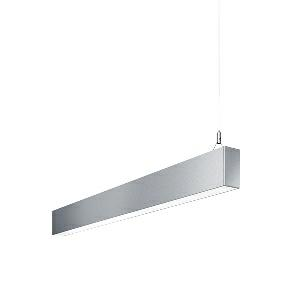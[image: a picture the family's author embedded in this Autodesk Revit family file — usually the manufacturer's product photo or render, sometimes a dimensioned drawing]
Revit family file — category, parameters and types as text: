
# Revit family: idoo_line_-_ilp_4000_vtl_d_end_00806471_4c60
name_source: partatom
category: Lighting Fixtures
units: mm (PartAtom-declared; Revit-internal decimal feet)

## family parameters
Cut with Voids When Loaded = No
Host = Face
Light Source = No
Part Type = Normal
Room Calculation Point = No
Round Connector Dimension = Use Diameter
Shared = No

## types (1)
- IDOO.line - ILP 4000/VTL/D END (1 x LED, 3850 lm, 2700-6500K)
    Apparent Load = 39 VA
    Approval mark = CE
    CIE Flux Codes = 66 91 98 40 100
    Color Rendering = 90-100
    Color Temperature = 2700-6500K
    Control Gear = Electronic ballast
    Default Elevation = 1800 mm
    Description = ILP 4000/VTL/D|Suspended luminaire|light source: LED|connected load: 220-240 V, 50/60 Hz|Power consumption: approx. 39 W|standby: approx. 0,25|luminous flux: 3850 lm|luminous efficacy: 98 lm/W|light distribution: Direct/indirect|direct ratio: approx. 40 %|colour temperature: Cold white, ca. 2700-6500 K|color rendering index (CRI): >= 90|chromaticity tolerance:  3 SDCM|System of protection: IP 40|technology: Continuously dimmable|luminaire body|material: Sectional aluminium|colour: Silver|lamp cover: Acrylic (PMMA), Clear|mains lead: 1,0 m With free stranded wires|Fastening: Steel cable 0.3 - 0.7 m|glare control: Prism aperture|luminance(L65): <= 2700 cd/m|unified glare rating(4H 8H): <=  16|special features: Specified values at approx. 4000 K, DALI Load 1x, Through-wired, up to 18 m on one mains connection, External control required for Dali Device type 8, Flicker-free, Constant luminous flux between 2700 and 6500 K, Constant colour temperature over the whole dimming range, Suitable as emergency lighting, Mechanical and electrical connection of the individual modules without tools|
    Frequency = 50 Hz
    Height = 110 mm
    Lamp = 1 x LED
    Lamp Light Flux = 3850 lm
    Lamp count = 1
    Length = 1408 mm
    Luminous efficacy = 99 lm/W
    Manufacturer = Waldmann
    ModVariant = No
    Model = 00806471
    Mounting Place = Ceiling
    Mounting Type = Pendant
    Number of Poles = 1
    OnlyDefault = Yes
    Power Factor = 1
    Product Name = IDOO.line - ILP 4000/VTL/D END
    Product group = Suspended luminaire
    ProductGroupID = 9
    Protection Class = Protection class I
    Protection Degree = IP 40
    RLX_Detail_Level = 1
    RLX_Emergency_Light_Flux = 0 lm
    RLX_Emergency_Type = 0
    RLX_Emergency_Type_DB = No
    RlxData = <blob elided: 20989 chars, md5=b3f55696>
    Socket = socket
    Standby Power = 0 W
    System Light Flux = 3850 lm
    System Power = 39 W
    Type Comments = Product without accessories
    Type Image = 113312000-00692600.jpg
    URL = http://relux.com
    VarID = ---
    Voltage = 230 V
    Voltage Range = 220-240 V
    Weight = 0.00 kg
    Width = 60 mm  [stored 0.19685 ft]

note: [stored X ft] marks values corroborated as IEEE doubles in the binary element streams (Revit-internal decimal feet)

## geometry (parser evidence)
native form markers: Blend x4, Sweep x13
no freeform markers — native parametric forms only
